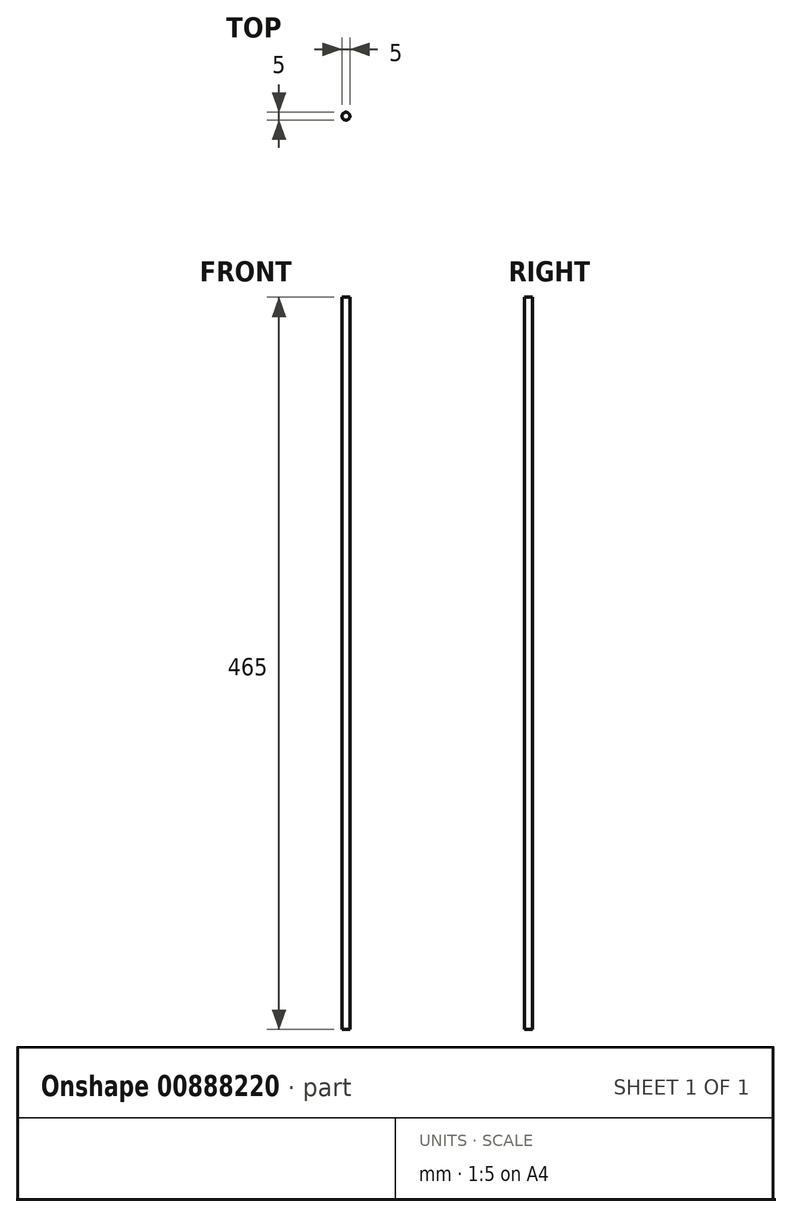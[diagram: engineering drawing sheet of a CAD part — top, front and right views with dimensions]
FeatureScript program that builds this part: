
annotation { "Feature Type Name" : "Feature", "Feature Type Description" : "" }
export const myFeature = defineFeature(function(context is Context, id is Id, definition is map)
    precondition{}
    {
        {
            var Q0;
            Q0=qCreatedBy(makeId("Top.planeOp"),FACE);
            var sketch = newSketch(context, id + "F0", { "sketchPlane" : qUnion([Q0])});
            skCircle(sketch, "E0", {"center": v(0, 0) * mm, "radius": 2.5 * mm});
            skSolve(sketch);
        }
        {
            var Q0;
            Q0 = qSketchRegion(id + "F0", true);
            extrude(context, id + "F1", {"entities" : qUnion([Q0]), "depth" : 465 * mm, "offsetDistance" : 25 * mm});
        }
    });
